# Revit family: FU_Seat_Sandler_Hyppo 8-4
name_source: partatom
category: Furniture
units: mm (PartAtom-declared; Revit-internal decimal feet)

## family parameters
Always vertical = Yes
Cut with Voids When Loaded = No
OmniClass Number = 23.40.20.00
OmniClass Title = General Furniture and Specialties
Room Calculation Point = No
Shared = No
Work Plane-Based = No

## types (1)
- Hyppo 8.4
    Default Elevation = 0 mm  [stored 0 ft]
    Depth = 570 mm  [stored 1.87008 ft]
    Description = Bench with upholstered seat on a solid beech frame.
    Height = 400 mm  [stored 1.31234 ft]
    Manufacturer = Sandler
    Model = Hyppo 8.4
    URL = https://www.sandlerseating.com
    Upholstery = Fabric - Gravity - Wheat CPC21
    Width = 1420 mm  [stored 4.65879 ft]
    Wood Finish = Wood - Stain - Canaletto

note: [stored X ft] marks values corroborated as IEEE doubles in the binary element streams (Revit-internal decimal feet)

## geometry (parser evidence)
native form markers: Sweep x3
no freeform markers — native parametric forms only
